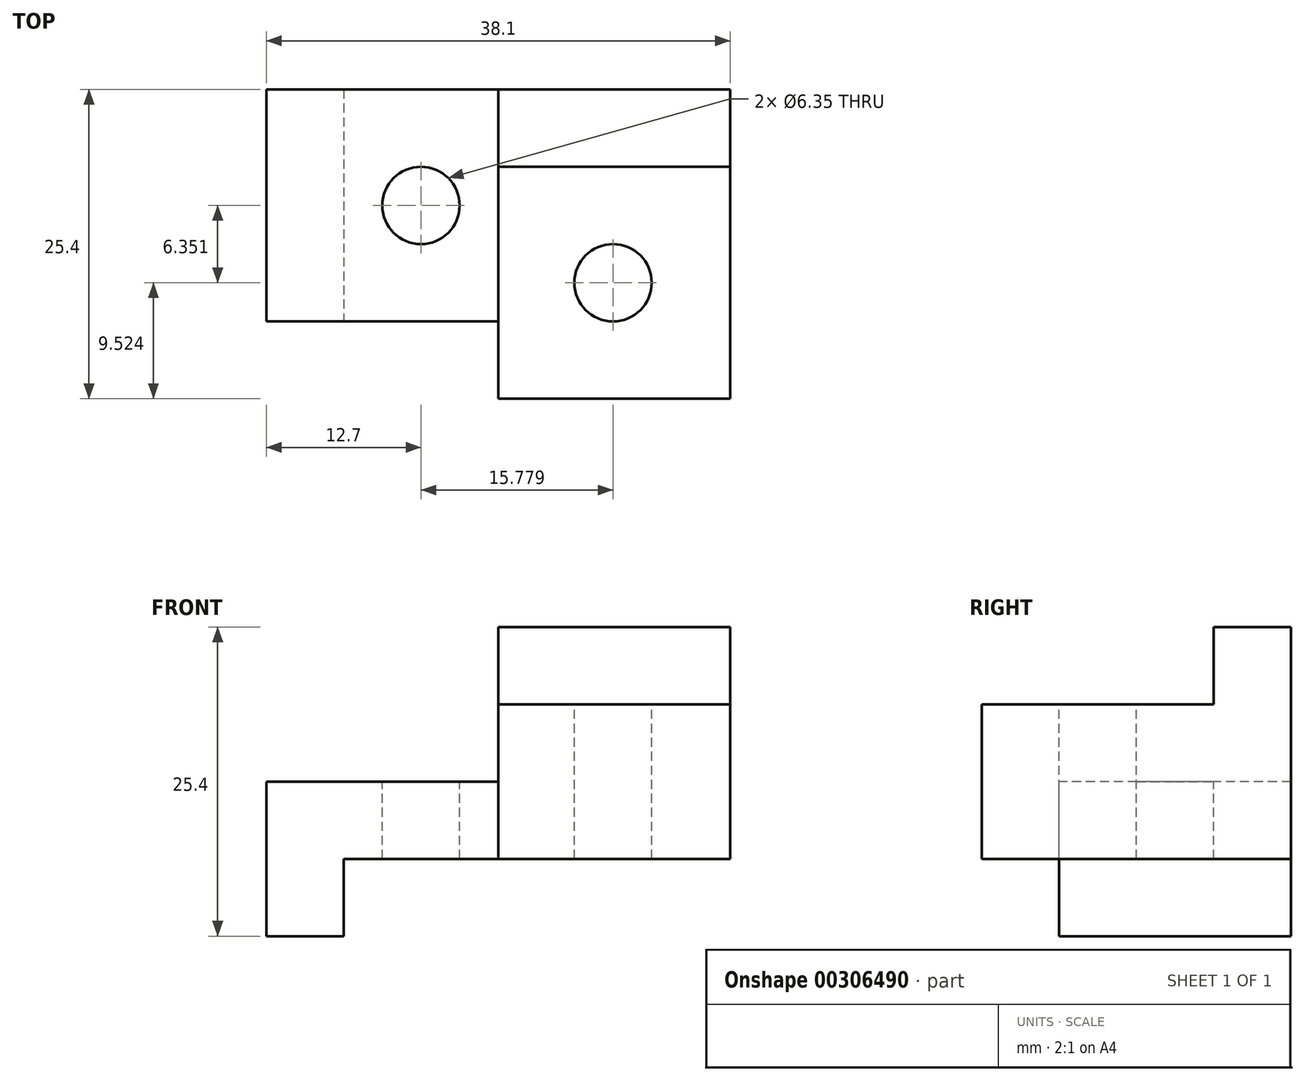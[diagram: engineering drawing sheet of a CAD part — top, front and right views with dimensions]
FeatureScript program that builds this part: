
annotation { "Feature Type Name" : "Feature", "Feature Type Description" : "" }
export const myFeature = defineFeature(function(context is Context, id is Id, definition is map)
    precondition{}
    {
        {
            var Q0;
            Q0=qCreatedBy(makeId("Front.planeOp"),FACE);
            var sketch = newSketch(context, id + "F0", { "sketchPlane" : qUnion([Q0])});
            skLineSegment(sketch, "E0.bottom", {"start": v(0, 0) * mm, "end": v(6.35, 0) * mm});
            skLineSegment(sketch, "E0.top", {"start": v(0, 12.7) * mm, "end": v(19.05, 12.7) * mm});
            skLineSegment(sketch, "E0.left", {"start": v(0, 0) * mm, "end": v(0, 12.7) * mm});
            skLineSegment(sketch, "E0.right", {"start": v(19.05, 6.35) * mm, "end": v(19.05, 12.7) * mm});
            skLineSegment(sketch, "E1.top", {"start": v(19.05, 6.35) * mm, "end": v(6.35, 6.35) * mm});
            skLineSegment(sketch, "E1.right", {"start": v(6.35, 0) * mm, "end": v(6.35, 6.35) * mm});
            skSolve(sketch);
        }
        {
            var Q0;
            Q0=makeQuery(id+"F0.imprint","IMPRINT",FACE,{"disambiguationData":[TD([[makeQuery(id+"F0.imprint","IMPRINT",EDGE,{"derivedFrom":sQuery(id+"F0.wireOp",EDGE,"E0.bottom")}),1.0]])]});
            extrude(context, id + "F1", {"entities" : qUnion([Q0]), "oppositeDirection" : true, "depth" : 19.05 * mm});
        }
        {
            var Q0;
            Q0=makeQuery(id+"F1.opExtrude","SWEPT_FACE",FACE,{"disambiguationData":[OSD([sQuery(id+"F0.wireOp",EDGE,"E0.top")])]});
            var sketch = newSketch(context, id + "F2", { "sketchPlane" : qUnion([Q0])});
            skCircle(sketch, "E2", {"center": v(12.7, 9.53) * mm, "radius": 3.18 * mm});
            skSolve(sketch);
        }
        {
            var Q0;
            Q0=makeQuery(id+"F2.imprint","IMPRINT",FACE,{"disambiguationData":[TD([[makeQuery(id+"F2.imprint","IMPRINT",EDGE,{"derivedFrom":sQuery(id+"F2.wireOp",EDGE,"E2")}),1.0]])]});
            extrude(context, id + "F3", {"entities" : qUnion([Q0]), "operationType" : NewBodyOperationType.REMOVE, "endBound" : BoundingType.THROUGH_ALL, "oppositeDirection" : true, "depth" : 25.4 * mm});
        }
        {
            var Q0;
            Q0=makeQuery(id+"F1.opExtrude","SWEPT_FACE",FACE,{"disambiguationData":[OSD([sQuery(id+"F0.wireOp",EDGE,"E0.right")])]});
            var sketch = newSketch(context, id + "F4", { "sketchPlane" : qUnion([Q0])});
            skLineSegment(sketch, "E3", {"start": v(19.05, 25.4) * mm, "end": v(12.7, 25.4) * mm});
            skLineSegment(sketch, "E4", {"start": v(12.7, 25.4) * mm, "end": v(12.7, 19.05) * mm});
            skLineSegment(sketch, "E5", {"start": v(12.7, 19.05) * mm, "end": v(-6.35, 19.05) * mm});
            skLineSegment(sketch, "E6", {"start": v(19.05, 6.35) * mm, "end": v(-6.35, 6.35) * mm});
            skLineSegment(sketch, "E7", {"start": v(-6.35, 19.05) * mm, "end": v(-6.35, 6.35) * mm});
            skLineSegment(sketch, "E8", {"start": v(19.05, 25.4) * mm, "end": v(19.05, 6.35) * mm});
            skSolve(sketch);
        }
        {
            var Q0;
            {var subQ4=sQuery(id+"F4.wireOp",EDGE,"E3");Q0=makeQuery(id+"F4.imprint","IMPRINT",FACE,{"disambiguationData":[TD([[makeQuery(id+"F4.imprint","IMPRINT",EDGE,{"derivedFrom":subQ4}),1.0]])]});}
            var Q1;
            {var subQ1=sQuery(id+"F0.wireOp",EDGE,"E0.right");var subQ2=makeQuery(id+"F1.opExtrude","CAP_EDGE",EDGE,{"disambiguationData":[OSD([subQ1])],"isStart":true});Q1=makeQuery(id+"F4.imprint","IMPRINT",FACE,{"disambiguationData":[TD([[makeQuery(id+"F4.imprint","IMPRINT",EDGE,{"derivedFrom":subQ2}),-1.0]])]});}
            extrude(context, id + "F5", {"entities" : qUnion([Q0, Q1]), "operationType" : NewBodyOperationType.ADD, "depth" : 19.05 * mm});
        }
        {
            var Q0;
            Q0=makeQuery(id+"F5.opExtrude","SWEPT_FACE",FACE,{"disambiguationData":[OSD([sQuery(id+"F4.wireOp",EDGE,"E5")])]});
            var sketch = newSketch(context, id + "F6", { "sketchPlane" : qUnion([Q0])});
            skCircle(sketch, "E9", {"center": v(28.48, 3.17) * mm, "radius": 3.18 * mm});
            skPoint(sketch, "E9.second.point", {"position": v(28.58, 6.35) * mm});
            skPoint(sketch, "E9.third.point", {"position": v(31.57, 3.91) * mm});
            skSolve(sketch);
        }
        {
            var Q0;
            Q0=makeQuery(id+"F6.imprint","IMPRINT",FACE,{"disambiguationData":[TD([[makeQuery(id+"F6.imprint","IMPRINT",EDGE,{"derivedFrom":sQuery(id+"F6.wireOp",EDGE,"E9")}),1.0]])]});
            extrude(context, id + "F7", {"entities" : qUnion([Q0]), "operationType" : NewBodyOperationType.REMOVE, "endBound" : BoundingType.THROUGH_ALL, "oppositeDirection" : true, "depth" : 25.4 * mm});
        }
    });
